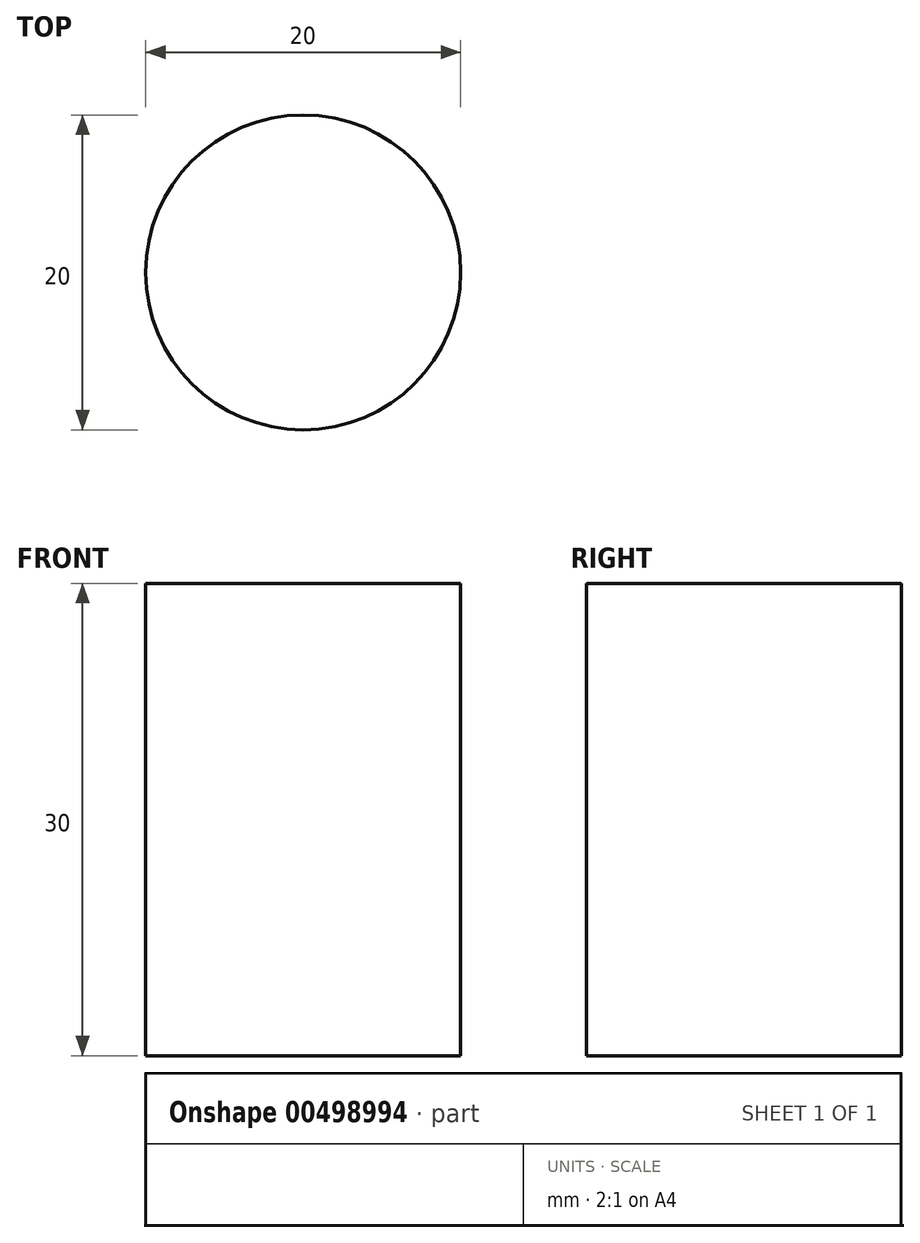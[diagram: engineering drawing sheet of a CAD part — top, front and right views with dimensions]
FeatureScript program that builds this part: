
annotation { "Feature Type Name" : "Feature", "Feature Type Description" : "" }
export const myFeature = defineFeature(function(context is Context, id is Id, definition is map)
    precondition{}
    {
        {
            var Q0;
            Q0=qCreatedBy(makeId("Top.planeOp"),FACE);
            var sketch = newSketch(context, id + "F0", { "sketchPlane" : qUnion([Q0])});
            skCircle(sketch, "E0", {"center": v(0, 0) * mm, "radius": 10 * mm});
            skSolve(sketch);
        }
        {
            var Q0;
            Q0 = qSketchRegion(id + "F0", true);
            extrude(context, id + "F1", {"entities" : qUnion([Q0]), "depth" : 30 * mm});
        }
    });
